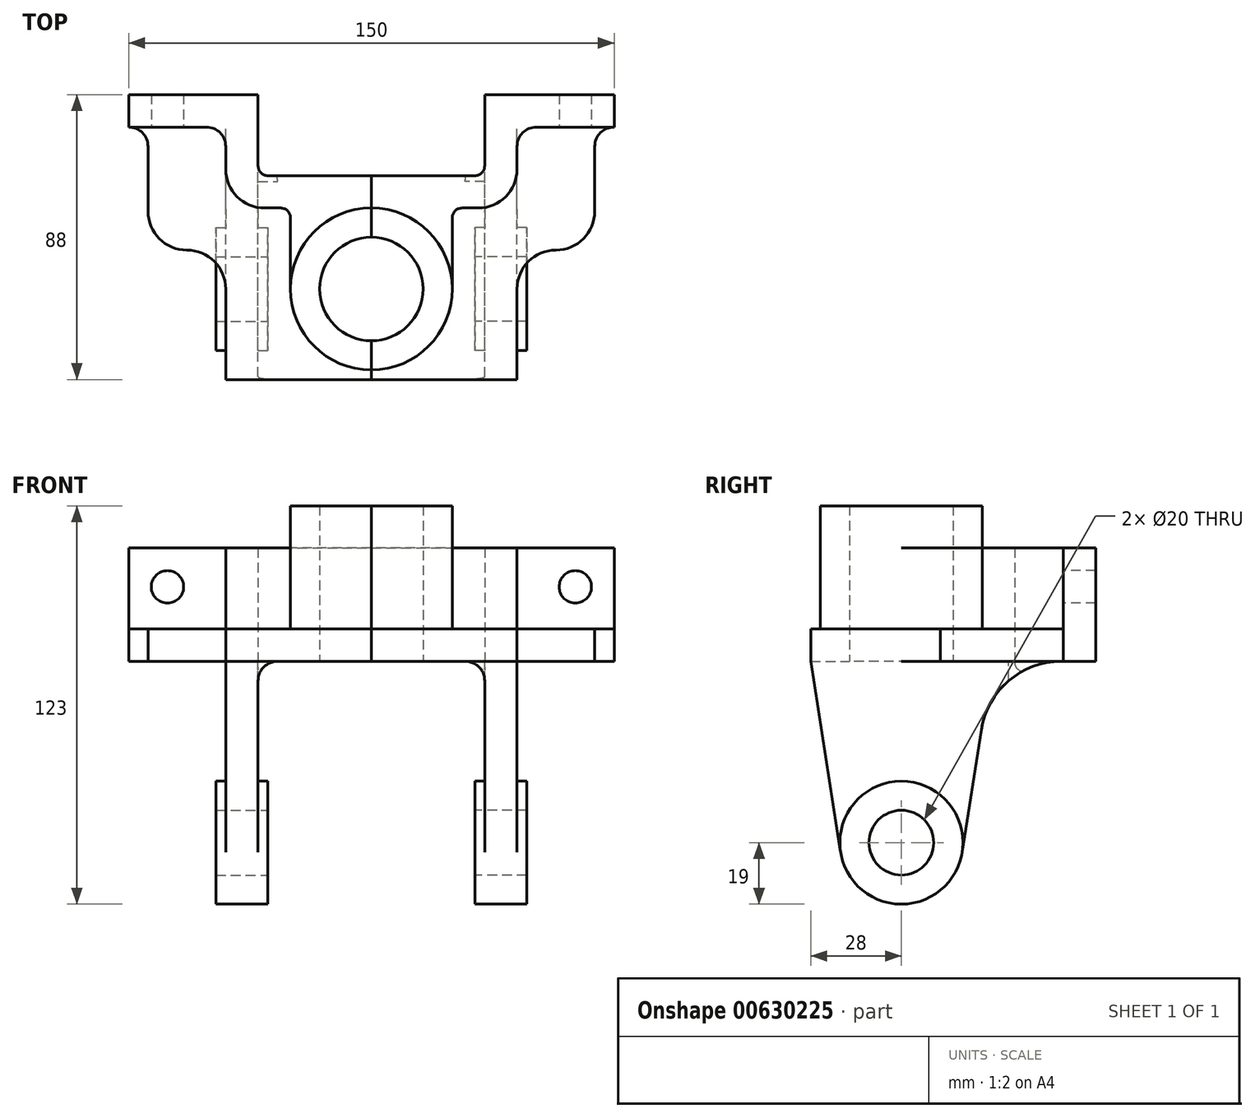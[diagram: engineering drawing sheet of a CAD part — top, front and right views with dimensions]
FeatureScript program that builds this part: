
annotation { "Feature Type Name" : "Feature", "Feature Type Description" : "" }
export const myFeature = defineFeature(function(context is Context, id is Id, definition is map)
    precondition{}
    {
        {
            var Q0;
            Q0=qCreatedBy(makeId("Top.planeOp"),FACE);
            var sketch = newSketch(context, id + "F0", { "sketchPlane" : qUnion([Q0])});
            skLineSegment(sketch, "E0", {"start": v(-75, 0) * mm, "end": v(-35, 0) * mm});
            skLineSegment(sketch, "E1.0", {"start": v(-32, -25) * mm, "end": v(0, -25) * mm});
            skLineSegment(sketch, "E2", {"start": v(-35, 0) * mm, "end": v(-35, -22) * mm});
            skLineSegment(sketch, "E3", {"start": v(-45, -16) * mm, "end": v(-45, -25) * mm});
            skLineSegment(sketch, "E4.0", {"start": v(-75, -10) * mm, "end": v(-75, -10) * mm});
            skLineSegment(sketch, "E5", {"start": v(-75, 0) * mm, "end": v(-75, -10) * mm});
            skLineSegment(sketch, "E6.0", {"start": v(-33, -35) * mm, "end": v(-28, -35) * mm});
            skLineSegment(sketch, "E7", {"start": v(-45, -23) * mm, "end": v(-45, -25) * mm});
            skLineSegment(sketch, "E8", {"start": v(0, 32.77) * mm, "end": v(0, -60) * mm});
            skArc(sketch, "E9", {"start": v(0, -44) * mm, "mid": v(-16, -60) * mm, "end": v(0, -76) * mm});
            skArc(sketch, "E10", {"start": v(0, -35) * mm, "mid": v(-25, -60) * mm, "end": v(0, -85) * mm});
            skLineSegment(sketch, "E11", {"start": v(-25, -38) * mm, "end": v(-25, -60) * mm});
            skArc(sketch, "E12.filletArc", {"start": v(-25, -38) * mm, "mid": v(-25.88, -35.88) * mm, "end": v(-28, -35) * mm});
            skPoint(sketch, "E13.visualSharp", {"position": v(-45, -10) * mm});
            skArc(sketch, "E13.filletArc", {"start": v(-45, -16) * mm, "mid": v(-46.76, -11.76) * mm, "end": v(-51, -10) * mm});
            skPoint(sketch, "E14.visualSharp", {"position": v(-45, -35) * mm});
            skArc(sketch, "E14.filletArc", {"start": v(-45, -23) * mm, "mid": v(-41.49, -31.49) * mm, "end": v(-33, -35) * mm});
            skPoint(sketch, "E15.visualSharp", {"position": v(-35, -25) * mm});
            skArc(sketch, "E15.filletArc", {"start": v(-35, -22) * mm, "mid": v(-34.12, -24.12) * mm, "end": v(-32, -25) * mm});
            skLineSegment(sketch, "E16", {"start": v(-45, -88) * mm, "end": v(0, -88) * mm});
            skLineSegment(sketch, "E17", {"start": v(-45, -88) * mm, "end": v(-45, -60) * mm});
            skLineSegment(sketch, "E18", {"start": v(-45, -60) * mm, "end": v(-45, -60) * mm});
            skLineSegment(sketch, "E19", {"start": v(-57, -48) * mm, "end": v(-57, -48) * mm});
            skLineSegment(sketch, "E20", {"start": v(-69, -36) * mm, "end": v(-69, -36) * mm});
            skLineSegment(sketch, "E21", {"start": v(-69, -36) * mm, "end": v(-69, -16) * mm});
            skArc(sketch, "E22.filletArc", {"start": v(-69, -16) * mm, "mid": v(-70.76, -11.76) * mm, "end": v(-75, -10) * mm});
            skPoint(sketch, "E23.visualSharp", {"position": v(-69, -48) * mm});
            skArc(sketch, "E23.filletArc", {"start": v(-69, -36) * mm, "mid": v(-65.49, -44.49) * mm, "end": v(-57, -48) * mm});
            skPoint(sketch, "E24.visualSharp", {"position": v(-45, -48) * mm});
            skArc(sketch, "E24.filletArc", {"start": v(-45, -60) * mm, "mid": v(-48.51, -51.51) * mm, "end": v(-57, -48) * mm});
            skLineSegment(sketch, "E25", {"start": v(-51, -10) * mm, "end": v(-75, -10) * mm});
            skLineSegment(sketch, "E26", {"start": v(0, -88) * mm, "end": v(0, -60) * mm});
            skSolve(sketch);
        }
        {
            var Q0;
            {var subQ6=sQuery(id+"F0.wireOp",EDGE,"E9");Q0=makeQuery(id+"F0.imprint","IMPRINT",FACE,{"disambiguationData":[TD([[makeQuery(id+"F0.imprint","IMPRINT",EDGE,{"derivedFrom":subQ6}),-1.0]])]});}
            extrude(context, id + "F1", {"entities" : qUnion([Q0]), "depth" : 38 * mm, "offsetDistance" : 25 * mm});
        }
        {
            var Q0;
            Q0=makeQuery(id+"F0.imprint","IMPRINT",FACE,{"disambiguationData":[TD([[makeQuery(id+"F0.imprint","IMPRINT",EDGE,{"derivedFrom":sQuery(id+"F0.wireOp",EDGE,"E0")}),-1.0]])]});
            extrude(context, id + "F2", {"entities" : qUnion([Q0]), "operationType" : NewBodyOperationType.ADD, "depth" : 25 * mm, "offsetDistance" : 25 * mm});
        }
        {
            var Q0;
            Q0=makeQuery(id+"F2.opExtrude","SWEPT_FACE",FACE,{"disambiguationData":[OSD([sQuery(id+"F0.wireOp",EDGE,"E25")])]});
            var sketch = newSketch(context, id + "F3", { "sketchPlane" : qUnion([Q0])});
            skCircle(sketch, "E27", {"center": v(-63, 13) * mm, "radius": 5 * mm});
            skSolve(sketch);
        }
        {
            var Q0;
            Q0=makeQuery(id+"F3.imprint","IMPRINT",FACE,{"disambiguationData":[TD([[makeQuery(id+"F3.imprint","IMPRINT",EDGE,{"derivedFrom":sQuery(id+"F3.wireOp",EDGE,"E27")}),1.0]])]});
            extrude(context, id + "F4", {"entities" : qUnion([Q0]), "operationType" : NewBodyOperationType.REMOVE, "oppositeDirection" : true, "depth" : 25 * mm, "offsetDistance" : 25 * mm});
        }
        {
            var Q0;
            Q0=makeQuery(id+"F0.imprint","IMPRINT",FACE,{"disambiguationData":[TD([[makeQuery(id+"F0.imprint","IMPRINT",EDGE,{"derivedFrom":sQuery(id+"F0.wireOp",EDGE,"E3")}),-1.0]])]});
            var Q1;
            Q1=makeQuery(id+"F0.imprint","IMPRINT",FACE,{"disambiguationData":[TD([[makeQuery(id+"F0.imprint","IMPRINT",EDGE,{"derivedFrom":sQuery(id+"F0.wireOp",EDGE,"E0")}),-1.0]])]});
            var Q2;
            {var subQ6=sQuery(id+"F0.wireOp",EDGE,"E9");Q2=makeQuery(id+"F0.imprint","IMPRINT",FACE,{"disambiguationData":[TD([[makeQuery(id+"F0.imprint","IMPRINT",EDGE,{"derivedFrom":subQ6}),-1.0]])]});}
            extrude(context, id + "F5", {"entities" : qUnion([Q0, Q1, Q2]), "operationType" : NewBodyOperationType.ADD, "oppositeDirection" : true, "depth" : 10 * mm, "offsetDistance" : 25 * mm});
        }
        {
            var Q0;
            Q0=makeQuery(id+"F5.opExtrude","SWEPT_FACE",FACE,{"disambiguationData":[OSD([sQuery(id+"F0.wireOp",EDGE,"E17")])]});
            var sketch = newSketch(context, id + "F6", { "sketchPlane" : qUnion([Q0])});
            skCircle(sketch, "E28", {"center": v(60, -66) * mm, "radius": 10 * mm});
            skCircle(sketch, "E29", {"center": v(60, -66) * mm, "radius": 19 * mm});
            skPoint(sketch, "E30.0", {"position": v(60, 38) * mm});
            skPoint(sketch, "E31.0", {"position": v(88, -10) * mm});
            skLineSegment(sketch, "E32", {"start": v(88, -10) * mm, "end": v(78.77, -68.94) * mm});
            skLineSegment(sketch, "E33", {"start": v(60, -66) * mm, "end": v(60, -20.85) * mm, "construction": true});
            skLineSegment(sketch, "E34.MirrorCS", {"start": v(35.3, -31.13) * mm, "end": v(41.23, -68.94) * mm});
            skLineSegment(sketch, "E35", {"start": v(10.6, -10) * mm, "end": v(0, -10) * mm});
            skPoint(sketch, "E36.visualSharp", {"position": v(32, -10) * mm});
            skArc(sketch, "E36.filletArc", {"start": v(35.3, -31.13) * mm, "mid": v(26.86, -16) * mm, "end": v(10.6, -10) * mm});
            skLineSegment(sketch, "E37", {"start": v(88, -10) * mm, "end": v(0, -10) * mm});
            skSolve(sketch);
        }
        {
            var Q0;
            {var subQ2=sQuery(id+"F6.wireOp",EDGE,"E32");Q0=makeQuery(id+"F6.imprint","IMPRINT",FACE,{"disambiguationData":[TD([[makeQuery(id+"F6.imprint","IMPRINT",EDGE,{"derivedFrom":subQ2}),-1.0]])]});}
            extrude(context, id + "F7", {"entities" : qUnion([Q0]), "operationType" : NewBodyOperationType.ADD, "oppositeDirection" : true, "depth" : 10 * mm, "offsetDistance" : 25 * mm});
        }
        {
            var Q0;
            Q0=makeQuery(id+"F6.imprint","IMPRINT",FACE,{"disambiguationData":[TD([[makeQuery(id+"F6.imprint","IMPRINT",EDGE,{"derivedFrom":sQuery(id+"F6.wireOp",EDGE,"E28")}),-1.0]])]});
            extrude(context, id + "F8", {"entities" : qUnion([Q0]), "depth" : 3 * mm, "offsetDistance" : 25 * mm});
        }
        {
            var Q0;
            Q0=makeQuery(id+"F6.imprint","IMPRINT",FACE,{"disambiguationData":[TD([[makeQuery(id+"F6.imprint","IMPRINT",EDGE,{"derivedFrom":sQuery(id+"F6.wireOp",EDGE,"E28")}),-1.0]])]});
            extrude(context, id + "F9", {"entities" : qUnion([Q0]), "operationType" : NewBodyOperationType.ADD, "oppositeDirection" : true, "depth" : 13 * mm, "offsetDistance" : 25 * mm});
        }
        {
            var Q0;
            Q0=makeQuery(id+"F7.opExtrude","CAP_EDGE",EDGE,{"disambiguationData":[OSD([sQuery(id+"F6.wireOp",EDGE,"E37")])],"isStart":false});
            fillet(context, id + "F10", {"entities" : qUnion([Q0]), "radius" : 6 * mm, "tangentPropagation" : true, "allowEdgeOverflow" : false});
        }
        {
            var Q0;
            Q0=makeQuery(id+"F1.opExtrude","SWEPT_BODY",BODY,{"disambiguationData":[OSD([sQuery(id+"F0.wireOp",EDGE,"E8"),sQuery(id+"F0.wireOp",EDGE,"E9"),sQuery(id+"F0.wireOp",EDGE,"E10"),sQuery(id+"F0.wireOp",EDGE,"E26")])]});
            var Q1;
            Q1=qCreatedBy(makeId("Right.planeOp"),FACE);
            mirror(context, id + "F11", {"entities" : qUnion([Q0]), "mirrorPlane" : qUnion([Q1])});
        }
    });
